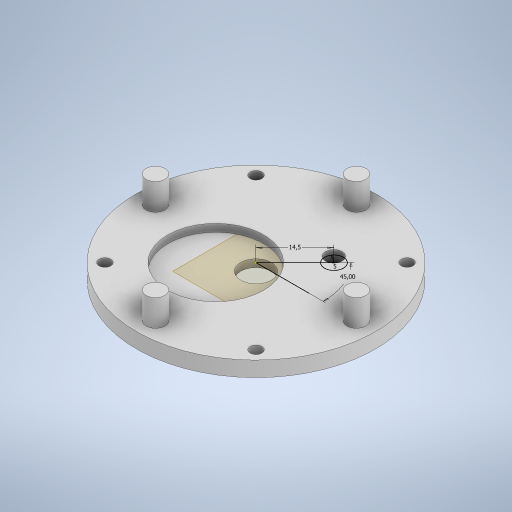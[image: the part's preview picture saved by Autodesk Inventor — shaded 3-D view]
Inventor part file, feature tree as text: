
AUTODESK INVENTOR PART (.ipt)
format: ipt  version: 2024 (Build 280153000, 153)  size: 310,784 bytes
history: native  units: in
note: dims shown in document units (in); Inventor stores cm internally (conversion verified against a paired STEP export)
features: sketch x9, extrude x6, plane x1
ambient origin geometry x8: Origin, YZ Plane, XZ Plane, XY Plane, X Axis, Y Axis, Z Axis, Center Point
bodies: Solid1 (feature_tree)
feature tree (16):
  extrude  "Plate"  Depth=0.1575in TaperAngle=0.0deg
  plane  "Work Plane1"
  extrude  "Camera hole"  Depth=0.1575in
  extrude  "Screw holes"  Depth=0.122in
  extrude  "Pillars"  Depth=0.1575in TaperAngle=0.0deg
  sketch  "Sketch6"  dims[d19=0.1969in d20=0.1929in]
  extrude  "Extrusion6"  Depth=0.1929in
  sketch  "Sketch8"  dims[d29=0.2953in]
  sketch  "Sketch9"  dims[d30=45.0deg]
  extrude  "Extrusion8"  Depth=0.2756in TaperAngle=0.0deg
  sketch  "Sketch1"  dims[d0=2.4803in d1=0.1575in d2=0.0in]
  sketch  "Sketch3"  dims[d7=0.1575in d8=0.0in d10=1.1087in]
  sketch  "Sketch4"  dims[d11=45.0deg d12=0.122in]
  sketch  "Sketch5"  dims[d13=1.5748in d15=360.0deg d17=0.1575in d18=0.0in]
  sketch  "Sketch7"  dims[d21=1.5748in d23=360.0deg d25=0.2756in d26=0.0in]
  sketch  "Sketch10"  dims[d31=0.9961in d32=0.0787in d33=0.0in d34=0.5709in d35=45.0deg d37=0.1969in d40=0.0787in d41=0.1732in d42=0.3937in d43=0.0in d50=0.3189in d27=0.0in d28=0.0in]
